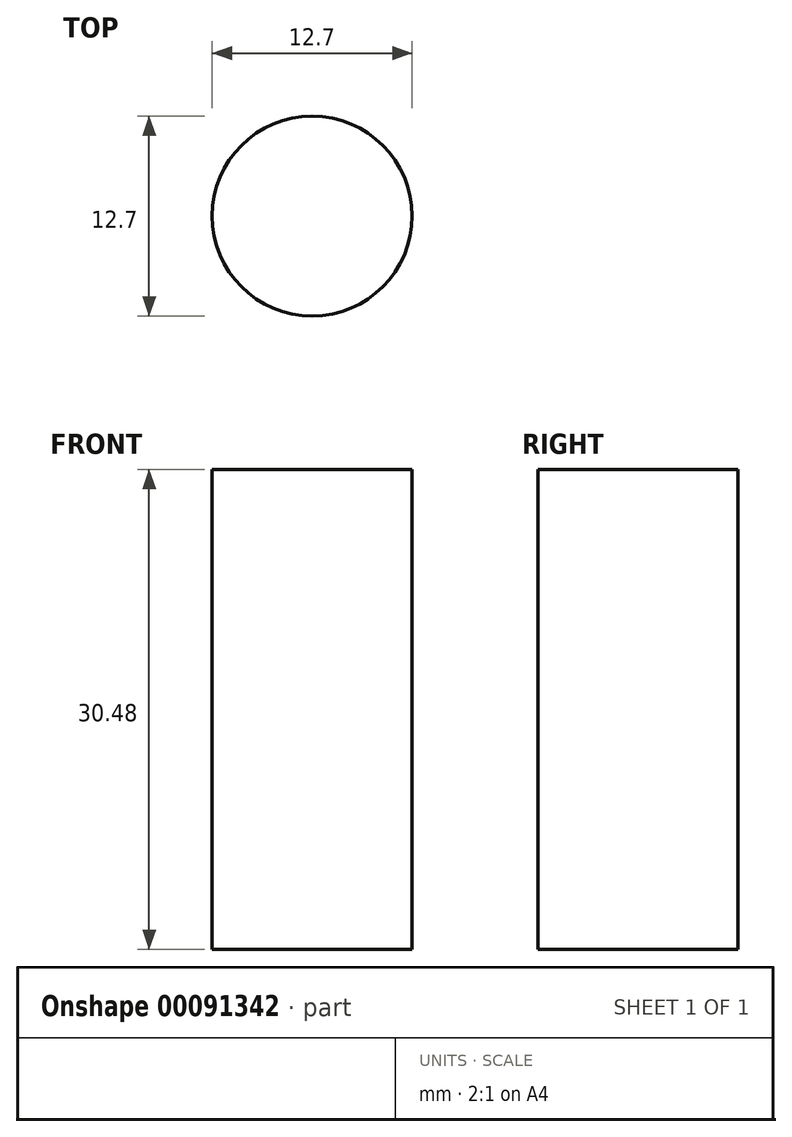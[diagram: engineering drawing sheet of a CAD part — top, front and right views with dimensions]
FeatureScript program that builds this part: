
annotation { "Feature Type Name" : "Feature", "Feature Type Description" : "" }
export const myFeature = defineFeature(function(context is Context, id is Id, definition is map)
    precondition{}
    {
        {
            var Q0;
            Q0=qCreatedBy(makeId("Top.planeOp"),FACE);
            var sketch = newSketch(context, id + "F0", { "sketchPlane" : qUnion([Q0])});
            skCircle(sketch, "E0", {"center": v(0, 0) * mm, "radius": 6.35 * mm});
            skSolve(sketch);
        }
        {
            var Q0;
            Q0=makeQuery(id+"F0.imprint","IMPRINT",FACE,{"disambiguationData":[TD([[makeQuery(id+"F0.imprint","IMPRINT",EDGE,{"derivedFrom":sQuery(id+"F0.wireOp",EDGE,"E0")}),1.0]])]});
            extrude(context, id + "F1", {"entities" : qUnion([Q0]), "depth" : 30.48 * mm});
        }
    });
